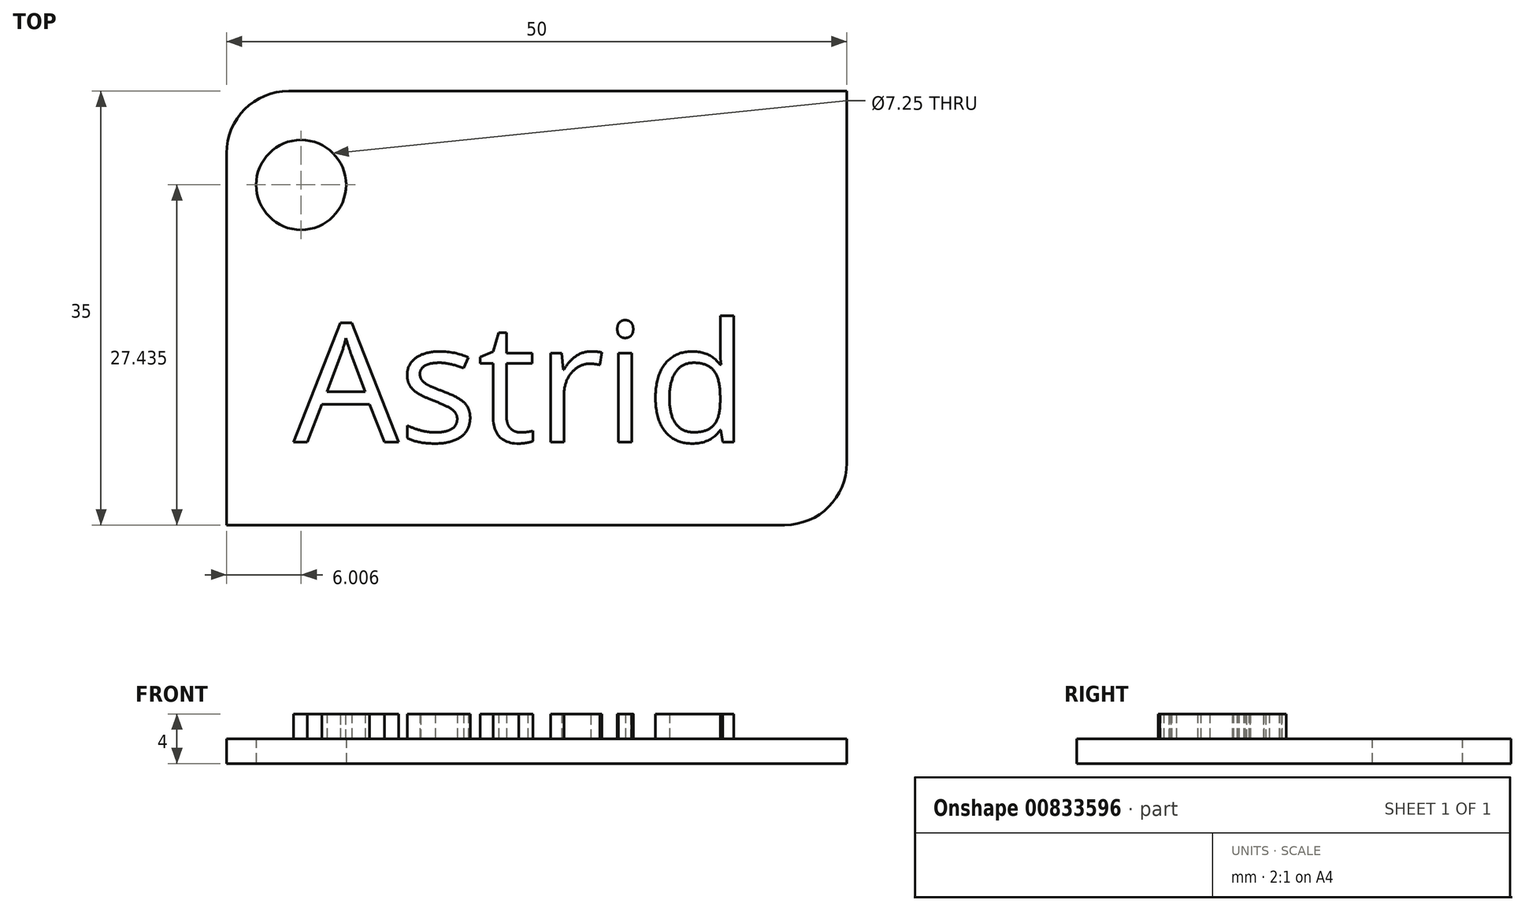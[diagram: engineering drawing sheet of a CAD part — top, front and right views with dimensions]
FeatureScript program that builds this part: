
annotation { "Feature Type Name" : "Feature", "Feature Type Description" : "" }
export const myFeature = defineFeature(function(context is Context, id is Id, definition is map)
    precondition{}
    {
        {
            var Q0;
            Q0=qCreatedBy(makeId("Top.planeOp"),FACE);
            var sketch = newSketch(context, id + "F0", { "sketchPlane" : qUnion([Q0])});
            skLineSegment(sketch, "E0.bottom", {"start": v(25, -17.5) * mm, "end": v(-25, -17.5) * mm});
            skLineSegment(sketch, "E0.top", {"start": v(25, 17.5) * mm, "end": v(-25, 17.5) * mm});
            skLineSegment(sketch, "E0.left", {"start": v(25, -17.5) * mm, "end": v(25, 17.5) * mm});
            skLineSegment(sketch, "E0.right", {"start": v(-25, -17.5) * mm, "end": v(-25, 17.5) * mm});
            skPoint(sketch, "E0.middle", {"position": v(0, 0) * mm});
            skCircle(sketch, "E1", {"center": v(-19, 9.94) * mm, "radius": 3.63 * mm});
            skSolve(sketch);
        }
        {
            var Q0;
            Q0 = qSketchRegion(id + "F0", true);
            extrude(context, id + "F1", {"entities" : qUnion([Q0]), "depth" : 2 * mm, "offsetDistance" : 25 * mm});
        }
        {
            var Q0;
            Q0=makeQuery(id+"F1.opExtrude","SWEPT_EDGE",EDGE,{"disambiguationData":[OSD([sQuery(id+"F0.wireOp",EDGE,"E0.top"),sQuery(id+"F0.wireOp",EDGE,"E0.right")])]});
            fillet(context, id + "F2", {"entities" : qUnion([Q0]), "radius" : 5 * mm, "tangentPropagation" : true, "allowEdgeOverflow" : false});
        }
        {
            var Q0;
            Q0=makeQuery(id+"F1.opExtrude","SWEPT_EDGE",EDGE,{"disambiguationData":[OSD([sQuery(id+"F0.wireOp",EDGE,"E0.bottom"),sQuery(id+"F0.wireOp",EDGE,"E0.left")])]});
            fillet(context, id + "F3", {"entities" : qUnion([Q0]), "radius" : 5 * mm, "tangentPropagation" : true, "allowEdgeOverflow" : false});
        }
        {
            var Q0;
            Q0=makeQuery(id+"F1.opExtrude","CAP_FACE",FACE,{"disambiguationData":[OSD([sQuery(id+"F0.wireOp",EDGE,"E0.bottom"),sQuery(id+"F0.wireOp",EDGE,"E0.top"),sQuery(id+"F0.wireOp",EDGE,"E0.left"),sQuery(id+"F0.wireOp",EDGE,"E0.right"),sQuery(id+"F0.wireOp",EDGE,"E1")])],"isStart":false});
            var sketch = newSketch(context, id + "F4", { "sketchPlane" : qUnion([Q0])});
            skText(sketch, "E2", { "text": "Astrid\n", "fontName": "OpenSans-Regular.ttf"});
            const initialGuessF4  = {"E2": [-0.01961, -0.0108, 1, 0, 0.00964]};
            skSetInitialGuess(sketch, initialGuessF4);
            skSolve(sketch);
        }
        {
            var Q0;
            Q0 = qSketchRegion(id + "F4", true);
            extrude(context, id + "F5", {"entities" : qUnion([Q0]), "operationType" : NewBodyOperationType.ADD, "depth" : 2 * mm, "offsetDistance" : 25 * mm});
        }
    });
